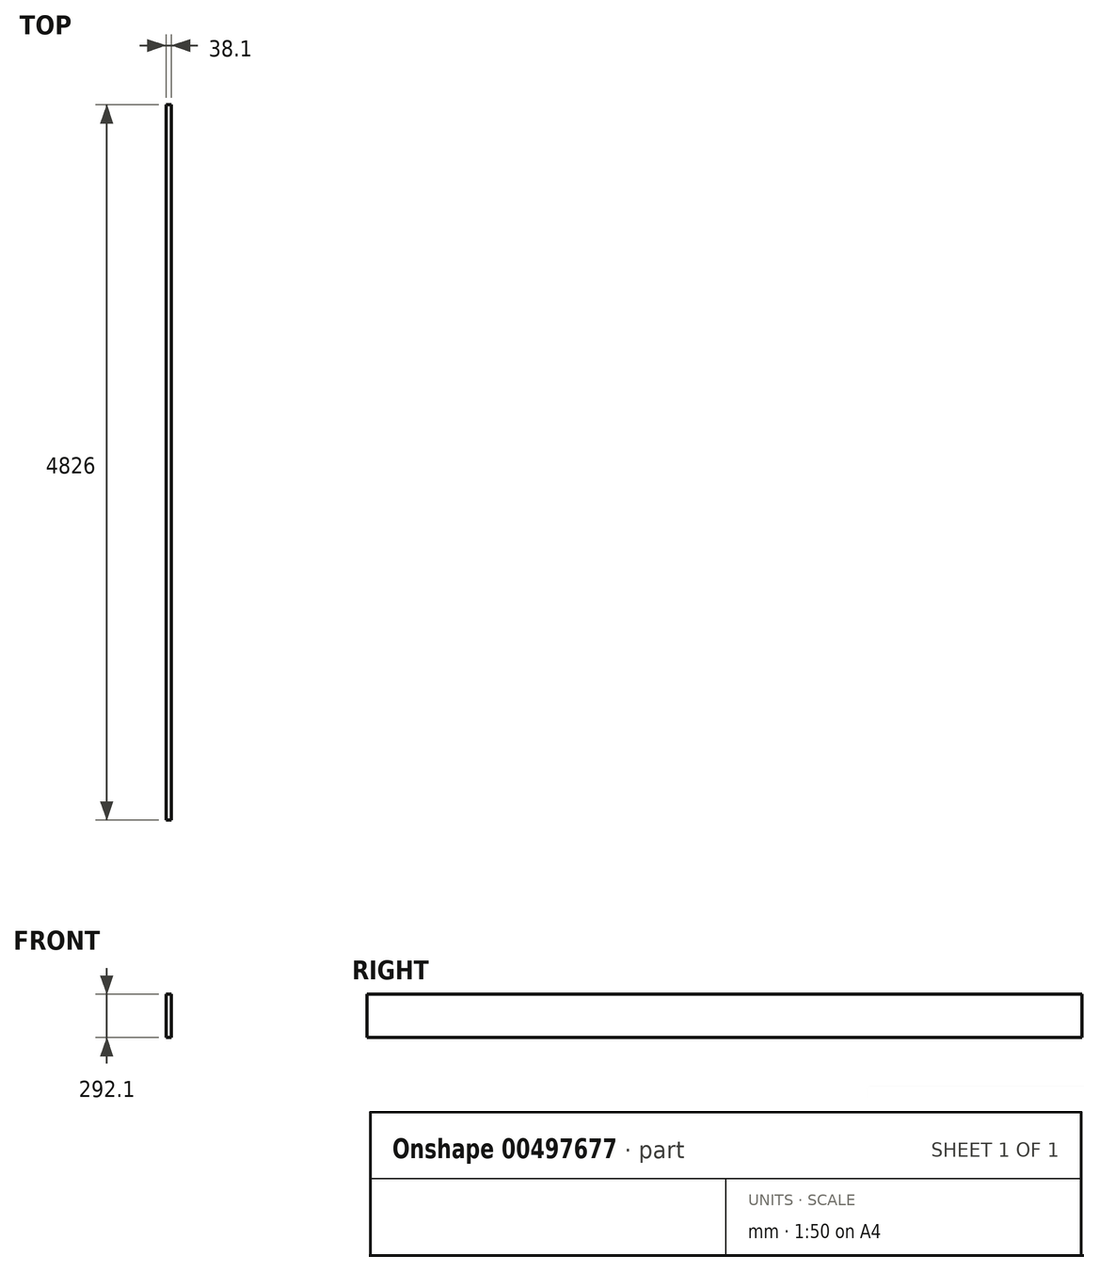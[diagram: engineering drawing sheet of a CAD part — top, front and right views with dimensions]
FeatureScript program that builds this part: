
annotation { "Feature Type Name" : "Feature", "Feature Type Description" : "" }
export const myFeature = defineFeature(function(context is Context, id is Id, definition is map)
    precondition{}
    {
        {
            var Q0;
            Q0=qCreatedBy(makeId("Front.planeOp"),FACE);
            var sketch = newSketch(context, id + "F0", { "sketchPlane" : qUnion([Q0])});
            skLineSegment(sketch, "E0.bottom", {"start": v(0, 0) * mm, "end": v(38.1, 0) * mm});
            skLineSegment(sketch, "E0.top", {"start": v(0, 292.1) * mm, "end": v(38.1, 292.1) * mm});
            skLineSegment(sketch, "E0.left", {"start": v(0, 0) * mm, "end": v(0, 292.1) * mm});
            skLineSegment(sketch, "E0.right", {"start": v(38.1, 0) * mm, "end": v(38.1, 292.1) * mm});
            skSolve(sketch);
        }
        {
            var Q0;
            Q0 = qSketchRegion(id + "F0", true);
            extrude(context, id + "F1", {"entities" : qUnion([Q0]), "depth" : 4826 * mm});
        }
    });
